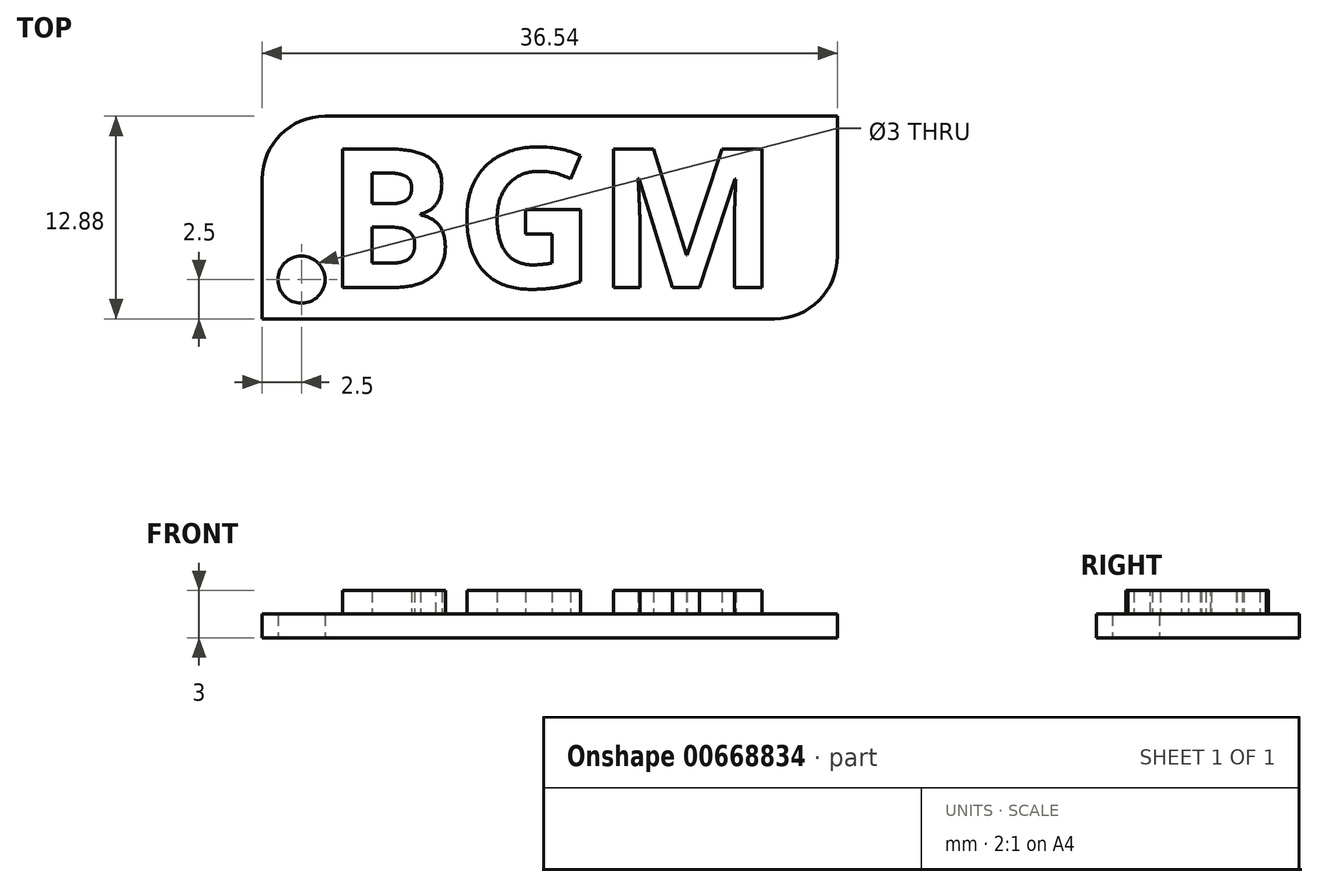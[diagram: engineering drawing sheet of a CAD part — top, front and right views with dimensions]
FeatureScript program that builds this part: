
annotation { "Feature Type Name" : "Feature", "Feature Type Description" : "" }
export const myFeature = defineFeature(function(context is Context, id is Id, definition is map)
    precondition{}
    {
        {
            var Q0;
            Q0=qCreatedBy(makeId("Top.planeOp"),FACE);
            var sketch = newSketch(context, id + "F0", { "sketchPlane" : qUnion([Q0])});
            skLineSegment(sketch, "E0.bottom", {"start": v(0, 0) * mm, "end": v(32.54, 0) * mm});
            skLineSegment(sketch, "E0.top", {"start": v(4, 12.88) * mm, "end": v(36.54, 12.88) * mm});
            skLineSegment(sketch, "E0.left", {"start": v(0, 0) * mm, "end": v(0, 8.88) * mm});
            skLineSegment(sketch, "E0.right", {"start": v(36.54, 4) * mm, "end": v(36.54, 12.88) * mm});
            skText(sketch, "E1", { "text": "BGM", "fontName": "OpenSans-Bold.ttf"});
            skPoint(sketch, "E2.visualSharp", {"position": v(0, 12.88) * mm});
            skArc(sketch, "E2.filletArc", {"start": v(4, 12.88) * mm, "mid": v(1.17, 11.71) * mm, "end": v(0, 8.88) * mm});
            skPoint(sketch, "E3.visualSharp", {"position": v(36.54, 0) * mm});
            skArc(sketch, "E3.filletArc", {"start": v(32.54, 0) * mm, "mid": v(35.37, 1.17) * mm, "end": v(36.54, 4) * mm});
            skCircle(sketch, "E4", {"center": v(2.5, 2.5) * mm, "radius": 1.5 * mm});
            const initialGuessF0  = {"E1": [0.004, 0.002, 1, 0, 0.00888]};
            skSetInitialGuess(sketch, initialGuessF0);
            skSolve(sketch);
        }
        {
            var Q0;
            Q0=makeQuery(id+"F0.imprint","IMPRINT",FACE,{"disambiguationData":[TD([[makeQuery(id+"F0.imprint","IMPRINT",EDGE,{"derivedFrom":sQuery(id+"F0.wireOp",EDGE,"E1.sketch_text.stroke-0")}),-1.0]])]});
            var Q1;
            Q1=makeQuery(id+"F0.imprint","IMPRINT",FACE,{"disambiguationData":[TD([[makeQuery(id+"F0.imprint","IMPRINT",EDGE,{"derivedFrom":sQuery(id+"F0.wireOp",EDGE,"E1.sketch_text.stroke-25")}),-1.0]])]});
            var Q2;
            Q2=makeQuery(id+"F0.imprint","IMPRINT",FACE,{"disambiguationData":[TD([[makeQuery(id+"F0.imprint","IMPRINT",EDGE,{"derivedFrom":sQuery(id+"F0.wireOp",EDGE,"E1.sketch_text.stroke-44")}),-1.0]])]});
            extrude(context, id + "F1", {"entities" : qUnion([Q0, Q1, Q2]), "depth" : 3 * mm, "offsetDistance" : 25 * mm});
        }
        {
            var Q0;
            Q0=makeQuery(id+"F0.imprint","IMPRINT",FACE,{"disambiguationData":[TD([[makeQuery(id+"F0.imprint","IMPRINT",EDGE,{"derivedFrom":sQuery(id+"F0.wireOp",EDGE,"E0.bottom")}),1.0]])]});
            var Q1;
            Q1=makeQuery(id+"F0.imprint","IMPRINT",FACE,{"disambiguationData":[TD([[makeQuery(id+"F0.imprint","IMPRINT",EDGE,{"derivedFrom":sQuery(id+"F0.wireOp",EDGE,"E1.sketch_text.stroke-19")}),1.0]])]});
            var Q2;
            Q2=makeQuery(id+"F0.imprint","IMPRINT",FACE,{"disambiguationData":[TD([[makeQuery(id+"F0.imprint","IMPRINT",EDGE,{"derivedFrom":sQuery(id+"F0.wireOp",EDGE,"E1.sketch_text.stroke-12")}),1.0]])]});
            extrude(context, id + "F2", {"entities" : qUnion([Q0, Q1, Q2]), "operationType" : NewBodyOperationType.ADD, "depth" : 1.5 * mm, "offsetDistance" : 25 * mm});
        }
    });
